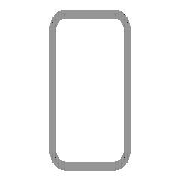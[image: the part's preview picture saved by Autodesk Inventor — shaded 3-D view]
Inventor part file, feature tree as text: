
AUTODESK INVENTOR PART (.ipt)
format: ipt  version: 2025 (Build 290162010, 162A)  size: 129,536 bytes
history: native  units: mm (DEFAULTED — no unit token found)
features: other x3, sketch x1, plane x1
ambient origin geometry x8: Origin, YZ Plane, XZ Plane, XY Plane, X Axis, Y Axis, Z Axis, Center Point
bodies: Solid1 (feature_tree), Body (feature_tree)
feature tree (5):
  other  "Driven Length"
  other  "Start plane"
  other  "End plane"
  sketch  "Sketch3"  dims[d3=160.0mm d4=0.0mm d7=4.0mm d9=20.0mm d11=40.0mm d12=2.0mm d13=-0.0mm d14=160.0mm d15=10.0mm d16=20.0mm d17=90.0deg d18=160.0mm]
  plane  "Work Plane3"
